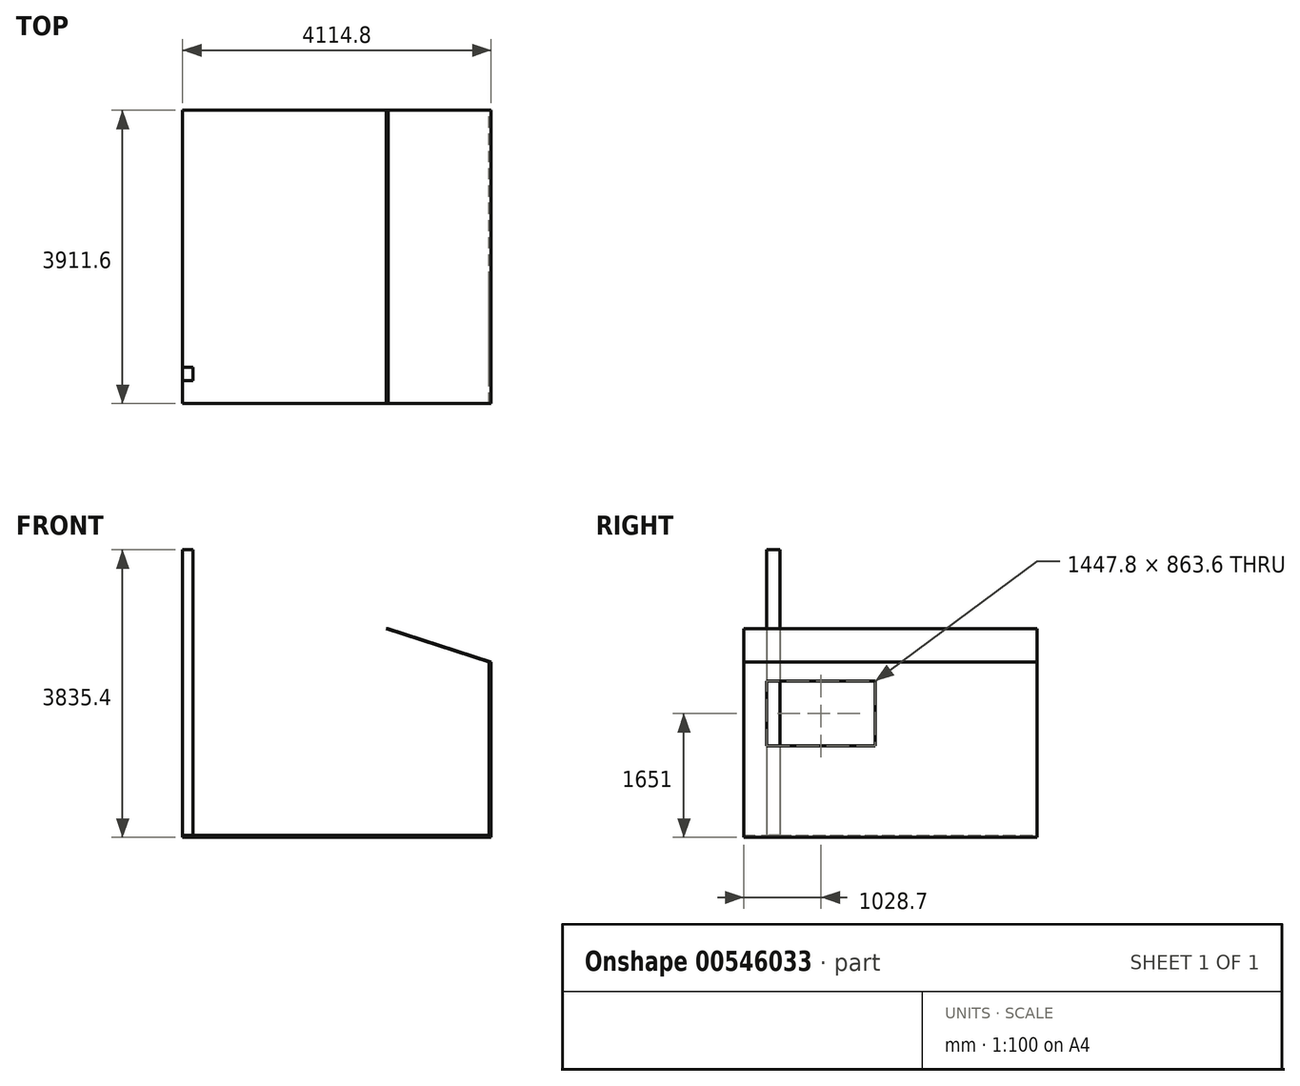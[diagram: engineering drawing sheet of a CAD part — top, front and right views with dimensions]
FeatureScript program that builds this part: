
annotation { "Feature Type Name" : "Feature", "Feature Type Description" : "" }
export const myFeature = defineFeature(function(context is Context, id is Id, definition is map)
    precondition{}
    {
        {
            var Q0;
            Q0=qCreatedBy(makeId("Top.planeOp"),FACE);
            var sketch = newSketch(context, id + "F0", { "sketchPlane" : qUnion([Q0])});
            skLineSegment(sketch, "E0.bottom", {"start": v(2057.4, -1955.8) * mm, "end": v(-2057.4, -1955.8) * mm});
            skLineSegment(sketch, "E0.top", {"start": v(2057.4, 1955.8) * mm, "end": v(-2057.4, 1955.8) * mm});
            skLineSegment(sketch, "E0.left", {"start": v(2057.4, -1955.8) * mm, "end": v(2057.4, 1955.8) * mm});
            skLineSegment(sketch, "E0.right", {"start": v(-2057.4, -1955.8) * mm, "end": v(-2057.4, 1955.8) * mm});
            skPoint(sketch, "E0.middle", {"position": v(0, 0) * mm});
            skSolve(sketch);
        }
        {
            var Q0;
            Q0 = qSketchRegion(id + "F0", true);
            extrude(context, id + "F1", {"entities" : qUnion([Q0]), "oppositeDirection" : true, "depth" : 25.4 * mm, "offsetDistance" : 25.4 * mm});
        }
        {
            var Q0;
            Q0=makeQuery(id+"F1.opExtrude","CAP_FACE",FACE,{"disambiguationData":[OSD([sQuery(id+"F0.wireOp",EDGE,"E0.bottom"),sQuery(id+"F0.wireOp",EDGE,"E0.top"),sQuery(id+"F0.wireOp",EDGE,"E0.left"),sQuery(id+"F0.wireOp",EDGE,"E0.right")])],"isStart":true});
            var sketch = newSketch(context, id + "F2", { "sketchPlane" : qUnion([Q0])});
            skLineSegment(sketch, "E1.bottom", {"start": v(2057.4, -1955.8) * mm, "end": v(2032, -1955.8) * mm});
            skLineSegment(sketch, "E1.top", {"start": v(2057.4, 1955.8) * mm, "end": v(2032, 1955.8) * mm});
            skLineSegment(sketch, "E1.left", {"start": v(2057.4, -1955.8) * mm, "end": v(2057.4, 1955.8) * mm});
            skLineSegment(sketch, "E1.right", {"start": v(2032, -1955.8) * mm, "end": v(2032, 1955.8) * mm});
            skSolve(sketch);
        }
        {
            var Q0;
            Q0 = qSketchRegion(id + "F2", true);
            extrude(context, id + "F3", {"entities" : qUnion([Q0]), "operationType" : NewBodyOperationType.ADD, "depth" : 2311.4 * mm, "offsetDistance" : 25.4 * mm});
        }
        {
            var Q0;
            Q0=makeQuery(id+"F3.boolean.opBoolean","MERGE",FACE,{"derivedFrom":[makeQuery(id+"F1.opExtrude","SWEPT_FACE",FACE,{"disambiguationData":[OSD([sQuery(id+"F0.wireOp",EDGE,"E0.left")])]}),makeQuery(id+"F3.opExtrude","SWEPT_FACE",FACE,{"disambiguationData":[OSD([sQuery(id+"F2.wireOp",EDGE,"E1.left")])]})]});
            var sketch = newSketch(context, id + "F4", { "sketchPlane" : qUnion([Q0])});
            skLineSegment(sketch, "E2.bottom", {"start": v(-1651, 2057.4) * mm, "end": v(-203.2, 2057.4) * mm});
            skLineSegment(sketch, "E2.top", {"start": v(-1651, 1193.8) * mm, "end": v(-203.2, 1193.8) * mm});
            skLineSegment(sketch, "E2.left", {"start": v(-1651, 2057.4) * mm, "end": v(-1651, 1193.8) * mm});
            skLineSegment(sketch, "E2.right", {"start": v(-203.2, 2057.4) * mm, "end": v(-203.2, 1193.8) * mm});
            skSolve(sketch);
        }
        {
            var Q0;
            Q0 = qSketchRegion(id + "F4", true);
            extrude(context, id + "F5", {"entities" : qUnion([Q0]), "operationType" : NewBodyOperationType.REMOVE, "oppositeDirection" : true, "depth" : 25.4 * mm, "offsetDistance" : 25.4 * mm});
        }
        {
            var Q0;
            Q0=makeQuery(id+"F1.opExtrude","CAP_FACE",FACE,{"disambiguationData":[OSD([sQuery(id+"F0.wireOp",EDGE,"E0.bottom"),sQuery(id+"F0.wireOp",EDGE,"E0.top"),sQuery(id+"F0.wireOp",EDGE,"E0.left"),sQuery(id+"F0.wireOp",EDGE,"E0.right")])],"isStart":true});
            var sketch = newSketch(context, id + "F6", { "sketchPlane" : qUnion([Q0])});
            skLineSegment(sketch, "E3.bottom", {"start": v(-2057.4, -1473.2) * mm, "end": v(-1917.7, -1473.2) * mm});
            skLineSegment(sketch, "E3.top", {"start": v(-2057.4, -1651) * mm, "end": v(-1917.7, -1651) * mm});
            skLineSegment(sketch, "E3.left", {"start": v(-2057.4, -1473.2) * mm, "end": v(-2057.4, -1651) * mm});
            skLineSegment(sketch, "E3.right", {"start": v(-1917.7, -1473.2) * mm, "end": v(-1917.7, -1651) * mm});
            skSolve(sketch);
        }
        {
            var Q0;
            Q0 = qSketchRegion(id + "F6", true);
            extrude(context, id + "F7", {"entities" : qUnion([Q0]), "operationType" : NewBodyOperationType.ADD, "depth" : 3810 * mm, "offsetDistance" : 25.4 * mm});
        }
        {
            var Q0;
            Q0=makeQuery(id+"F3.boolean.opBoolean","MERGE",FACE,{"derivedFrom":[makeQuery(id+"F1.opExtrude","SWEPT_FACE",FACE,{"disambiguationData":[OSD([sQuery(id+"F0.wireOp",EDGE,"E0.bottom")])]}),makeQuery(id+"F3.opExtrude","SWEPT_FACE",FACE,{"disambiguationData":[OSD([sQuery(id+"F2.wireOp",EDGE,"E1.bottom")])]})]});
            var sketch = newSketch(context, id + "F8", { "sketchPlane" : qUnion([Q0])});
            skLineSegment(sketch, "E4", {"start": v(2032, 2311.4) * mm, "end": v(660.62, 2756.99) * mm});
            skLineSegment(sketch, "E5", {"start": v(660.62, 2756.99) * mm, "end": v(686.02, 2756.99) * mm});
            skLineSegment(sketch, "E6", {"start": v(686.02, 2756.99) * mm, "end": v(2057.4, 2311.4) * mm});
            skLineSegment(sketch, "E7", {"start": v(2057.4, 2311.4) * mm, "end": v(2032, 2311.4) * mm});
            skLineSegment(sketch, "E8", {"start": v(2032, 2311.4) * mm, "end": v(1637.42, 2311.4) * mm, "construction": true});
            skSolve(sketch);
        }
        {
            var Q0;
            Q0 = qSketchRegion(id + "F8", true);
            var Q1;
            Q1=makeQuery(id+"F3.boolean.opBoolean","MERGE",FACE,{"derivedFrom":[makeQuery(id+"F1.opExtrude","SWEPT_FACE",FACE,{"disambiguationData":[OSD([sQuery(id+"F0.wireOp",EDGE,"E0.top")])]}),makeQuery(id+"F3.opExtrude","SWEPT_FACE",FACE,{"disambiguationData":[OSD([sQuery(id+"F2.wireOp",EDGE,"E1.top")])]})]});
            extrude(context, id + "F9", {"entities" : qUnion([Q0]), "operationType" : NewBodyOperationType.ADD, "endBound" : BoundingType.UP_TO_SURFACE, "oppositeDirection" : true, "depth" : 25.4 * mm, "endBoundEntityFace" : qUnion([Q1]), "offsetDistance" : 25.4 * mm});
        }
    });
